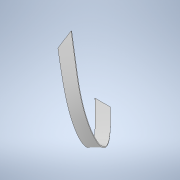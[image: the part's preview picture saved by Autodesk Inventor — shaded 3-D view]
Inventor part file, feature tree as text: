
AUTODESK INVENTOR PART (.ipt)
format: ipt  version: 2021 (Build 250183000, 183)  size: 170,496 bytes
history: native  units: in
note: dims shown in document units (in); Inventor stores cm internally (conversion verified against a paired STEP export)
features: sketch x2, sweep x1
ambient origin geometry x8: Origin, YZ Plane, XZ Plane, XY Plane, X Axis, Y Axis, Z Axis, Center Point
bodies: Body1 (feature_tree)
feature tree (3):
  sweep  "Sweep2"
  sketch  "3D Sketch1"
  sketch  "Sketch2"  dims[d12=0.1in d13=2.0in d14=0.0in d15=0.0in]
